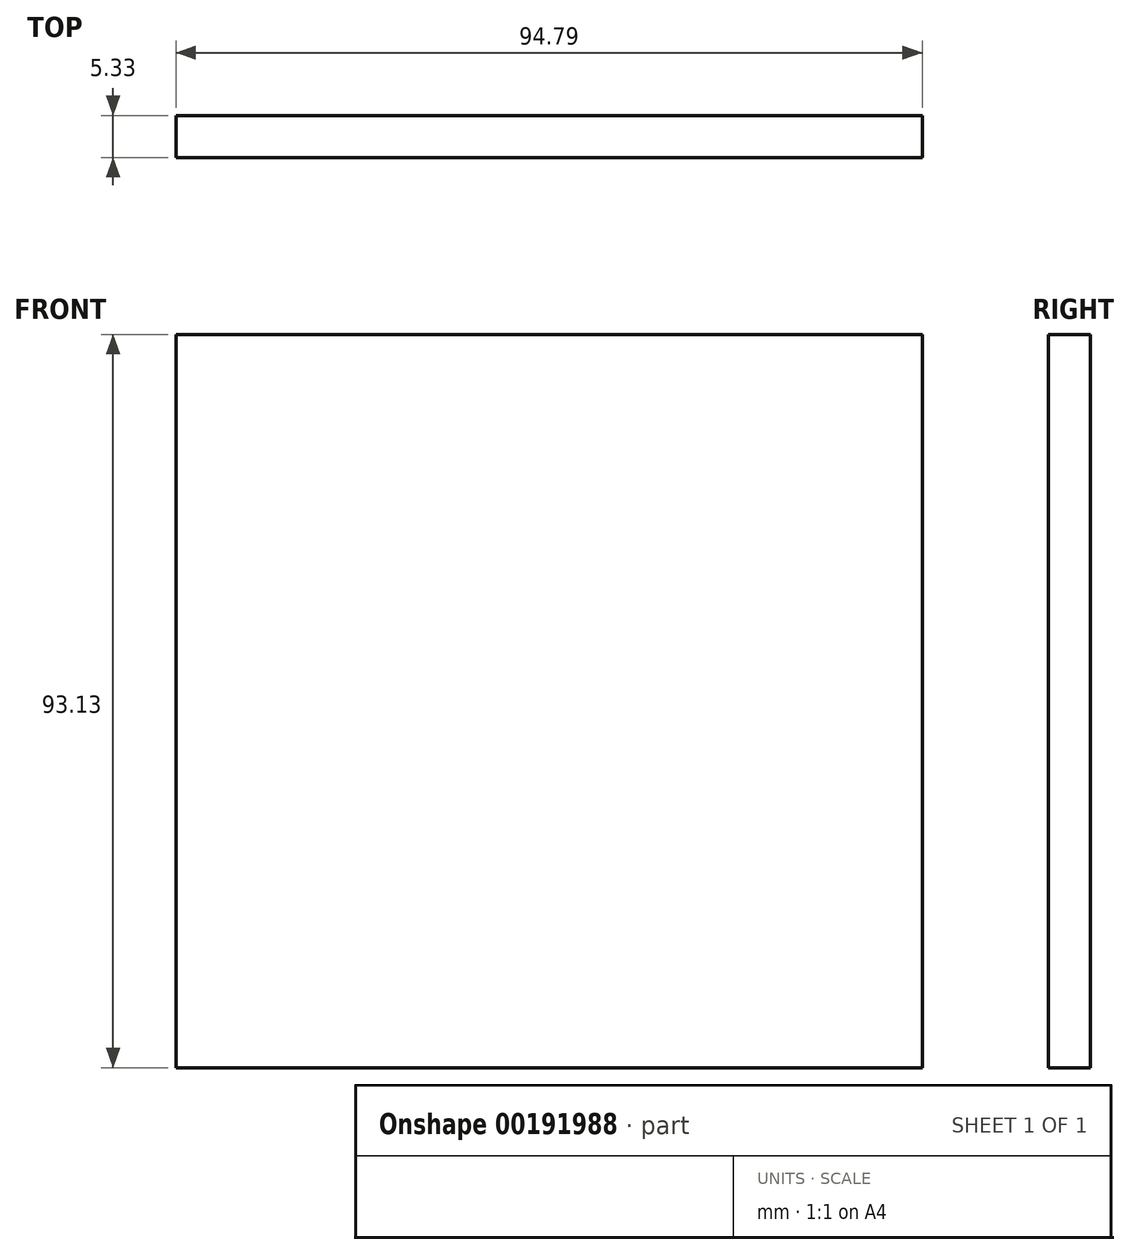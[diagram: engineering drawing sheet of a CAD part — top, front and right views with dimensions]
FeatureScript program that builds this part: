
annotation { "Feature Type Name" : "Feature", "Feature Type Description" : "" }
export const myFeature = defineFeature(function(context is Context, id is Id, definition is map)
    precondition{}
    {
        {
            var Q0;
            Q0=qCreatedBy(makeId("Front.planeOp"),FACE);
            var sketch = newSketch(context, id + "F0", { "sketchPlane" : qUnion([Q0])});
            skLineSegment(sketch, "E0", {"start": v(0, 0) * mm, "end": v(-94.79, 0) * mm});
            skLineSegment(sketch, "E1", {"start": v(-94.79, 0) * mm, "end": v(-94.79, 93.13) * mm});
            skLineSegment(sketch, "E2", {"start": v(-94.79, 93.13) * mm, "end": v(0, 93.13) * mm});
            skLineSegment(sketch, "E3", {"start": v(0, 93.13) * mm, "end": v(0, 0) * mm});
            skSolve(sketch);
        }
        {
            var Q0;
            Q0=makeQuery(id+"F0.imprint","IMPRINT",FACE,{"disambiguationData":[TD([[makeQuery(id+"F0.imprint","IMPRINT",EDGE,{"derivedFrom":sQuery(id+"F0.wireOp",EDGE,"E0")}),-1.0]])]});
            extrude(context, id + "F1", {"entities" : qUnion([Q0]), "depth" : 5.33 * mm});
        }
    });
